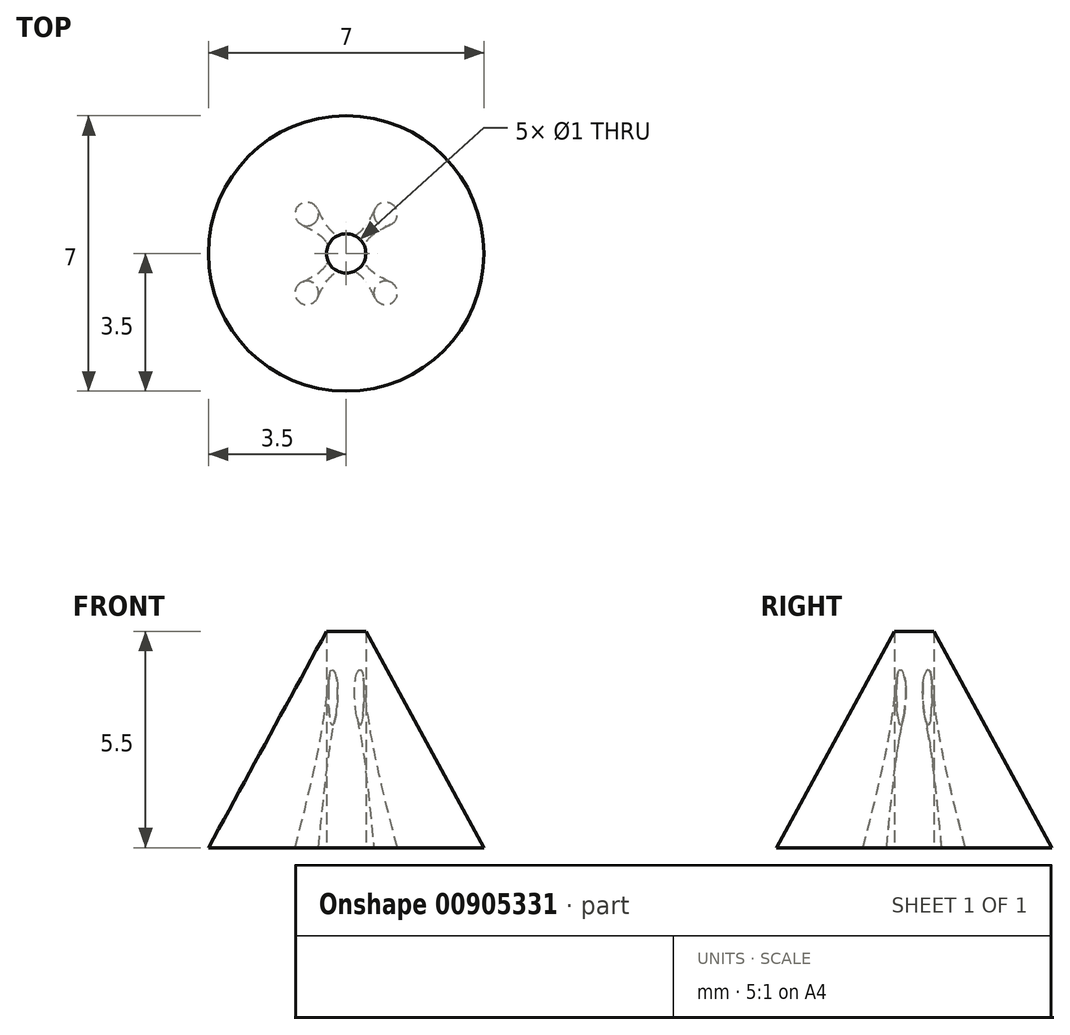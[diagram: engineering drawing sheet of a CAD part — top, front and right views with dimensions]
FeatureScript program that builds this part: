
annotation { "Feature Type Name" : "Feature", "Feature Type Description" : "" }
export const myFeature = defineFeature(function(context is Context, id is Id, definition is map)
    precondition{}
    {
        {
            var Q0;
            Q0=qCreatedBy(makeId("Front.planeOp"),FACE);
            var sketch = newSketch(context, id + "F0", { "sketchPlane" : qUnion([Q0])});
            skLineSegment(sketch, "E0", {"start": v(-0.5, 0) * mm, "end": v(-0.5, 5.5) * mm});
            skLineSegment(sketch, "E1", {"start": v(-0.5, 5.5) * mm, "end": v(-3.5, 0) * mm});
            skLineSegment(sketch, "E2", {"start": v(-3.5, 0) * mm, "end": v(-0.5, 0) * mm});
            skLineSegment(sketch, "E3", {"start": v(-0.5, 0) * mm, "end": v(0, 0) * mm});
            skLineSegment(sketch, "E4", {"start": v(0, 0) * mm, "end": v(0, 5.5) * mm});
            skLineSegment(sketch, "E5", {"start": v(0, 5.5) * mm, "end": v(-0.5, 5.5) * mm});
            skSolve(sketch);
        }
        {
            var Q0;
            Q0=makeQuery(id+"F0.imprint","IMPRINT",FACE,{"disambiguationData":[TD([[makeQuery(id+"F0.imprint","IMPRINT",EDGE,{"derivedFrom":sQuery(id+"F0.wireOp",EDGE,"E0")}),1.0]])]});
            var Q1;
            Q1=sQuery(id+"F0.wireOp",EDGE,"E4");
            revolve(context, id + "F1", {"surfaceOperationType" : NewSurfaceOperationType.NEW, "entities" : qUnion([Q0]), "axis" : qUnion([Q1]), "revolveType" : RevolveType.FULL});
        }
        {
            var Q0;
            Q0=makeQuery(id+"F1.opRevolve","SWEPT_FACE",FACE,{"disambiguationData":[OSD([sQuery(id+"F0.wireOp",EDGE,"E2")])]});
            var sketch = newSketch(context, id + "F2", { "sketchPlane" : qUnion([Q0])});
            skPoint(sketch, "E6.middle", {"position": v(0, 0) * mm});
            skCircle(sketch, "E7", {"center": v(-1, 1) * mm, "radius": 0.3 * mm});
            skCircle(sketch, "E8", {"center": v(1, 1) * mm, "radius": 0.3 * mm});
            skCircle(sketch, "E9", {"center": v(-1, -1) * mm, "radius": 0.3 * mm});
            skCircle(sketch, "E10", {"center": v(1, -1) * mm, "radius": 0.3 * mm});
            skLineSegment(sketch, "E11.bottom", {"start": v(1, -1) * mm, "end": v(-1, -1) * mm, "construction": true});
            skLineSegment(sketch, "E11.top", {"start": v(1, 1) * mm, "end": v(-1, 1) * mm, "construction": true});
            skLineSegment(sketch, "E11.left", {"start": v(1, -1) * mm, "end": v(1, 1) * mm, "construction": true});
            skLineSegment(sketch, "E11.right", {"start": v(-1, -1) * mm, "end": v(-1, 1) * mm, "construction": true});
            skSolve(sketch);
        }
        {
            var Q0;
            Q0=makeQuery(id+"F2.imprint","IMPRINT",FACE,{"disambiguationData":[TD([[makeQuery(id+"F2.imprint","IMPRINT",EDGE,{"derivedFrom":makeQuery(id+"F1.opRevolve","SWEPT_EDGE",EDGE,{"disambiguationData":[OSD([sQuery(id+"F0.wireOp",EDGE,"E0"),sQuery(id+"F0.wireOp",EDGE,"E2"),sQuery(id+"F0.wireOp",EDGE,"E3")])]})}),1.0]])]});
            cPlane(context, id + "F3", {"entities" : qUnion([Q0]), "cplaneType" : CPlaneType.OFFSET, "offset" : 5.7 * mm, "oppositeDirection" : true, "width" : 150 * mm, "height" : 150 * mm});
        }
        {
            var Q0;
            Q0=qCreatedBy(id+"F3.planeOp",FACE);
            var sketch = newSketch(context, id + "F4", { "sketchPlane" : qUnion([Q0])});
            skCircle(sketch, "E12", {"center": v(0, 0) * mm, "radius": 0.3 * mm});
            skSolve(sketch);
        }
        {
            var Q1;
            Q1=makeQuery(id+"F4.imprint","IMPRINT",FACE,{"disambiguationData":[TD([[makeQuery(id+"F4.imprint","IMPRINT",EDGE,{"derivedFrom":sQuery(id+"F4.wireOp",EDGE,"E12")}),1.0]])]});
            var Q2;
            Q2=makeQuery(id+"F2.imprint","IMPRINT",FACE,{"disambiguationData":[TD([[makeQuery(id+"F2.imprint","IMPRINT",EDGE,{"derivedFrom":sQuery(id+"F2.wireOp",EDGE,"E9")}),1.0]])]});
            loft(context, id + "F5", {"operationType" : NewBodyOperationType.REMOVE, "sheetProfilesArray" : [{ "sheetProfileEntities" : qUnion([Q1]) }, { "sheetProfileEntities" : qUnion([Q2]) }]});
        }
        {
            var Q0;
            Q0=makeQuery(id+"F4.imprint","IMPRINT",FACE,{"disambiguationData":[TD([[makeQuery(id+"F4.imprint","IMPRINT",EDGE,{"derivedFrom":sQuery(id+"F4.wireOp",EDGE,"E12")}),1.0]])]});
            var Q1;
            Q1=makeQuery(id+"F2.imprint","IMPRINT",FACE,{"disambiguationData":[TD([[makeQuery(id+"F2.imprint","IMPRINT",EDGE,{"derivedFrom":sQuery(id+"F2.wireOp",EDGE,"E7")}),1.0]])]});
            loft(context, id + "F6", {"operationType" : NewBodyOperationType.REMOVE, "sheetProfilesArray" : [{ "sheetProfileEntities" : qUnion([Q0]) }, { "sheetProfileEntities" : qUnion([Q1]) }]});
        }
        {
            var Q0;
            Q0=makeQuery(id+"F2.imprint","IMPRINT",FACE,{"disambiguationData":[TD([[makeQuery(id+"F2.imprint","IMPRINT",EDGE,{"derivedFrom":sQuery(id+"F2.wireOp",EDGE,"E8")}),1.0]])]});
            var Q1;
            Q1=makeQuery(id+"F4.imprint","IMPRINT",FACE,{"disambiguationData":[TD([[makeQuery(id+"F4.imprint","IMPRINT",EDGE,{"derivedFrom":sQuery(id+"F4.wireOp",EDGE,"E12")}),1.0]])]});
            loft(context, id + "F7", {"operationType" : NewBodyOperationType.REMOVE, "sheetProfilesArray" : [{ "sheetProfileEntities" : qUnion([Q0]) }, { "sheetProfileEntities" : qUnion([Q1]) }]});
        }
        {
            var Q0;
            Q0=makeQuery(id+"F2.imprint","IMPRINT",FACE,{"disambiguationData":[TD([[makeQuery(id+"F2.imprint","IMPRINT",EDGE,{"derivedFrom":sQuery(id+"F2.wireOp",EDGE,"E10")}),1.0]])]});
            var Q1;
            Q1=makeQuery(id+"F4.imprint","IMPRINT",FACE,{"disambiguationData":[TD([[makeQuery(id+"F4.imprint","IMPRINT",EDGE,{"derivedFrom":sQuery(id+"F4.wireOp",EDGE,"E12")}),1.0]])]});
            loft(context, id + "F8", {"operationType" : NewBodyOperationType.REMOVE, "sheetProfilesArray" : [{ "sheetProfileEntities" : qUnion([Q0]) }, { "sheetProfileEntities" : qUnion([Q1]) }]});
        }
    });
